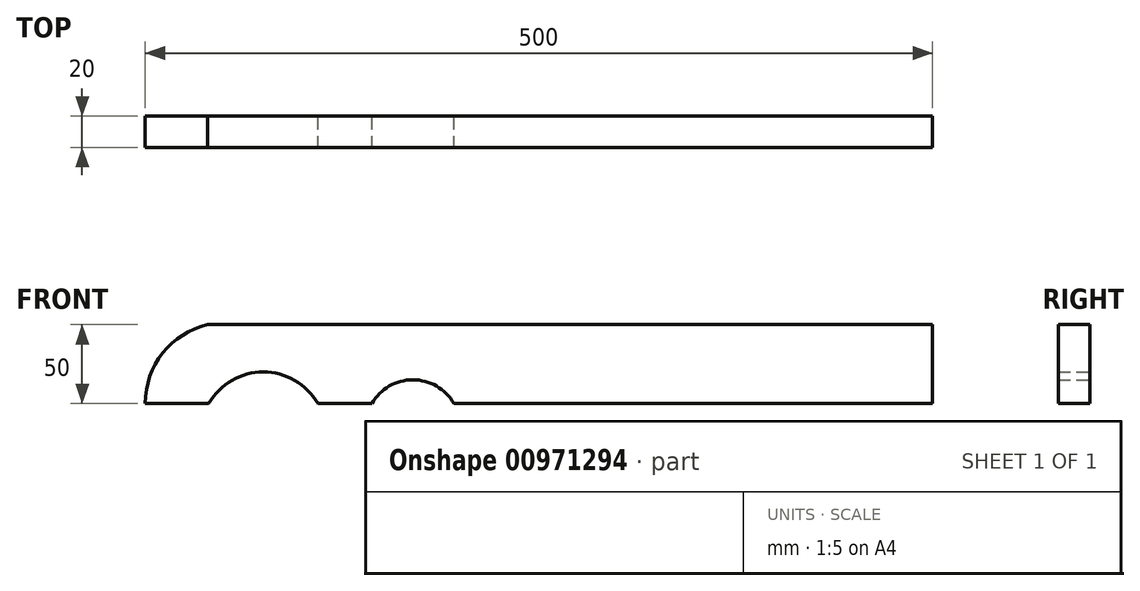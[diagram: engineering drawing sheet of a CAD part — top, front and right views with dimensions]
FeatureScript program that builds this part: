
annotation { "Feature Type Name" : "Feature", "Feature Type Description" : "" }
export const myFeature = defineFeature(function(context is Context, id is Id, definition is map)
    precondition{}
    {
        {
            var Q0;
            Q0=qCreatedBy(makeId("Front.planeOp"),FACE);
            var sketch = newSketch(context, id + "F0", { "sketchPlane" : qUnion([Q0])});
            skLineSegment(sketch, "E0.bottom", {"start": v(39.6, 0) * mm, "end": v(500, 0) * mm});
            skLineSegment(sketch, "E0.top", {"start": v(0, -50) * mm, "end": v(40.36, -50) * mm});
            skLineSegment(sketch, "E0.left", {"start": v(0, -50) * mm, "end": v(0, -50) * mm});
            skLineSegment(sketch, "E0.right", {"start": v(500, 0) * mm, "end": v(500, -50) * mm});
            skArc(sketch, "E1", {"start": v(40.36, -50) * mm, "mid": v(75, -30) * mm, "end": v(109.64, -50) * mm});
            skArc(sketch, "E2", {"start": v(144.02, -50) * mm, "mid": v(170, -35) * mm, "end": v(195.98, -50) * mm});
            skLineSegment(sketch, "E3.trimOffspring", {"start": v(109.64, -50) * mm, "end": v(144.02, -50) * mm});
            skArc(sketch, "E4", {"start": v(0, -50) * mm, "mid": v(11.1, -18.11) * mm, "end": v(39.6, 0) * mm});
            skLineSegment(sketch, "E5.trimOffspring", {"start": v(195.98, -50) * mm, "end": v(500, -50) * mm});
            skSolve(sketch);
        }
        {
            var Q0;
            Q0=makeQuery(id+"F0.imprint","IMPRINT",FACE,{"disambiguationData":[TD([[makeQuery(id+"F0.imprint","IMPRINT",EDGE,{"derivedFrom":sQuery(id+"F0.wireOp",EDGE,"E0.bottom")}),-1.0]])]});
            extrude(context, id + "F1", {"entities" : qUnion([Q0]), "depth" : 20 * mm, "offsetDistance" : 25 * mm});
        }
    });
